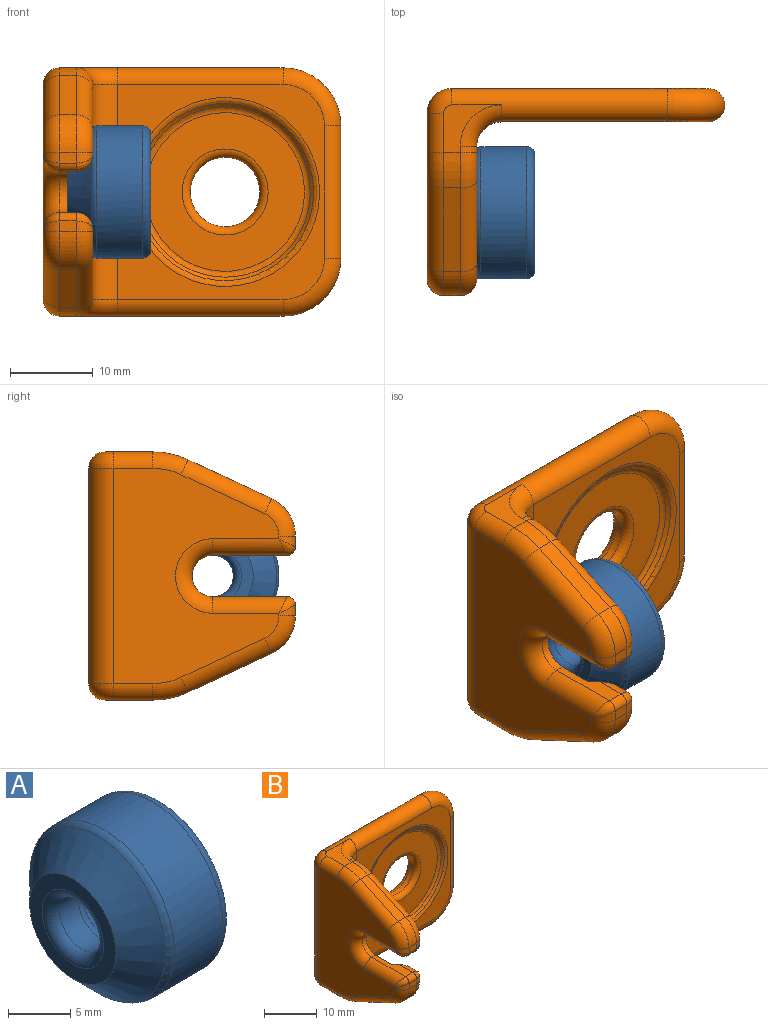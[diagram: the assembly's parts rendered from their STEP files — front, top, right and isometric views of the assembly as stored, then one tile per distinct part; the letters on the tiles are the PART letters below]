
ASSEMBLY  parts=2 mates=1
PART A: 12 faces, bbox 10x17.3x17.3 mm
  f0: cylinder r=2.5mm len=5mm, axis (-1,0,0), area 33.4mm2, adj f10,f11
  f1: cylinder r=8mm len=16mm, axis (-1,0,0), area 275.7mm2, adj f8,f9
  f2: plane 14x14mm, normal (1,0,0), area 21.2mm2, adj f7,f9
  f3: plane 9.8x9.8mm, normal (-1,0,0), area 36.9mm2, adj f4,f11
  f4: cone r=8mm half-angle=45deg, axis (1,0,0), area 157.2mm2, adj f3,f8
  f5: cylinder r=5.5mm len=11mm, axis (1,0,0), area 69.1mm2, adj f6,f7
  f6: torus R=2.5mm, axis (1,0,0), area 116.9mm2, adj f5,f10
  f7: torus R=6.5mm, axis (1,0,0), area 57.9mm2, adj f2,f5
  f8: torus R=7mm, axis (-1,0,0), area 39mm2, adj f1,f4
  f9: torus R=7mm, axis (1,0,0), area 75.4mm2, adj f1,f2
  f10: torus R=3.5mm, axis (-1,0,0), area 22.9mm2, adj f0,f6
  f11: torus R=3.5mm, axis (1,0,0), area 28.3mm2, adj f0,f3
PART B: 69 faces, bbox 36.6x25.5x31.7 mm
  f0: plane 16x13mm, normal (1,0,0), area 62.4mm2, adj f17,f18,f41,f42,f43,f44,f45,f47
  f1: plane 2x1.32mm, normal (0,-1,0), area 2.6mm2, adj f21,f23,f45,f60
  f2: plane 2x1.32mm, normal (0,-1,0), area 2.6mm2, adj f22,f24,f29,f57
  f3: plane 16x13mm, normal (1,0,0), area 62.4mm2, adj f17,f18,f27,f29,f30,f31,f32,f33
  f4: plane 7x5.78mm, normal (0,0,1), area 16.7mm2, adj f20,f33,f34,f35,f48,f49
  f5: plane 7x5.78mm, normal (0,0,-1), area 16.7mm2, adj f19,f39,f40,f41,f50,f52
  f6: plane 26x20mm, normal (-1,0,0), area 330.1mm2, adj f26,f49,f51,f52,f53,f54,f55,f56
  f7: plane 31x26mm, normal (0,1,0), area 710.3mm2, adj f26,f35,f36,f37,f38,f39,f66
  f8: plane 26x25mm, normal (0,-1,0), area 230mm2, adj f18,f35,f36,f37,f38,f39,f65
  f9: plane 19.17x19.17mm, normal (0,-1,0), area 203.7mm2, adj f67,f68
  f10: cylinder r=4.2mm len=8.4mm, axis (0,-1,0), area 26.4mm2, adj f66,f67
  f11: plane 10.1x4.72mm, normal (0,-0.42,-0.91), area 22.3mm2, adj f19,f21,f43,f56
  f12: plane 10.1x4.72mm, normal (0,-0.42,0.91), area 22.3mm2, adj f20,f22,f31,f53
  f13: plane 10x9.33mm, normal (1,0,0), area 44.8mm2, adj f14,f15,f16,f17
  f14: plane 9.05x2.05mm, normal (0,0,1), area 13.1mm2, adj f13,f15,f17,f23,f47,f64
  f15: cylinder r=2.5mm len=5mm, axis (1,0,0), area 7.9mm2, adj f13,f14,f16,f63
  f16: plane 9.05x2.05mm, normal (0,0,-1), area 13.1mm2, adj f13,f15,f17,f24,f27,f61
  f17: cone r=5mm half-angle=45deg, axis (1,0,0), area 148.8mm2, adj f0,f3,f13,f14,f16,f27,f47
  f18: cylinder r=3mm len=26mm, axis (0,0,-1), area 122.5mm2, adj f0,f3,f8,f34,f40
  f19: cylinder r=10mm len=4.23mm, axis (-1,0,0), area 8.7mm2, adj f5,f11,f42,f54
  f20: cylinder r=10mm len=4.23mm, axis (1,0,0), area 8.7mm2, adj f4,f12,f32,f51
  f21: cylinder r=5mm len=4.53mm, axis (1,0,0), area 11.3mm2, adj f1,f11,f44,f58
  f22: cylinder r=5mm len=4.53mm, axis (1,0,0), area 11.3mm2, adj f2,f12,f30,f55
  f23: cylinder r=1mm len=2mm, axis (-1,0,0), area 3.1mm2, adj f1,f14,f46,f62
  f24: cylinder r=1mm len=2mm, axis (1,0,0), area 3.1mm2, adj f2,f16,f28,f59
  f25: cone r=10mm half-angle=45deg, axis (0,-1,0), area 38.6mm2, adj f65,f68
  f26: cylinder r=3mm len=26mm, axis (0,0,-1), area 122.5mm2, adj f6,f7,f48,f50
  f27: cylinder r=2mm len=3.55mm, axis (0,1,0), area 6.7mm2, adj f3,f16,f17,f28
  f28: bspline ~2.1x2mm, area 3.3mm2, adj f24,f27,f29
  f29: cylinder r=2mm len=2mm, axis (0,0,-1), area 3mm2, adj f2,f3,f28,f30
  f30: torus R=3mm, axis (1,0,0), area 15.2mm2, adj f3,f22,f29,f31
  f31: cylinder r=2mm len=10.95mm, axis (0,-0.91,-0.42), area 35mm2, adj f3,f12,f30,f32
  f32: torus R=8mm, axis (1,0,0), area 12.7mm2, adj f3,f20,f31,f33
  f33: cylinder r=2mm len=2mm, axis (0,-1,0), area 2.5mm2, adj f3,f4,f32,f34
  f34: torus R=5mm, axis (0,0,1), area 18.4mm2, adj f4,f18,f33,f35
  f35: cylinder r=2mm len=26mm, axis (-1,0,0), area 144.5mm2, adj f4,f7,f8,f34,f36,f48
  f36: torus R=5mm, axis (0,1,0), area 61.9mm2, adj f7,f8,f35,f37
  f37: cylinder r=2mm len=16mm, axis (0,0,-1), area 100.5mm2, adj f7,f8,f36,f38
  f38: torus R=5mm, axis (0,1,0), area 61.9mm2, adj f7,f8,f37,f39
  f39: cylinder r=2mm len=26mm, axis (1,0,0), area 144.5mm2, adj f5,f7,f8,f38,f40,f50
  f40: torus R=5mm, axis (0,0,1), area 18.4mm2, adj f5,f18,f39,f41
  f41: cylinder r=2mm len=2mm, axis (0,1,0), area 2.5mm2, adj f0,f5,f40,f42
  f42: torus R=8mm, axis (1,0,0), area 12.7mm2, adj f0,f19,f41,f43
  f43: cylinder r=2mm len=10.95mm, axis (0,-0.91,0.42), area 35mm2, adj f0,f11,f42,f44
  f44: torus R=3mm, axis (1,0,0), area 15.2mm2, adj f0,f21,f43,f45
  f45: cylinder r=2mm len=2mm, axis (0,0,-1), area 3mm2, adj f0,f1,f44,f46
  f46: bspline ~2.1x2mm, area 3.3mm2, adj f23,f45,f47
  f47: cylinder r=2mm len=3.55mm, axis (0,-1,0), area 6.7mm2, adj f0,f14,f17,f46
  f48: torus R=1mm, axis (0,0,1), area 11.2mm2, adj f4,f26,f35,f49
  f49: cylinder r=2mm len=4.78mm, axis (0,1,0), area 15mm2, adj f4,f6,f48,f51
  f50: torus R=1mm, axis (0,0,1), area 11.2mm2, adj f5,f26,f39,f52
  f51: torus R=8mm, axis (1,0,0), area 12.7mm2, adj f6,f20,f49,f53
  f52: cylinder r=2mm len=4.78mm, axis (0,-1,0), area 15mm2, adj f5,f6,f50,f54
  f53: cylinder r=2mm len=10.95mm, axis (0,0.91,0.42), area 35mm2, adj f6,f12,f51,f55
  f54: torus R=8mm, axis (1,0,0), area 12.7mm2, adj f6,f19,f52,f56
  f55: torus R=3mm, axis (1,0,0), area 15.2mm2, adj f6,f22,f53,f57
  f56: cylinder r=2mm len=10.95mm, axis (0,-0.91,0.42), area 35mm2, adj f6,f11,f54,f58
  f57: cylinder r=2mm len=2mm, axis (0,0,1), area 3mm2, adj f2,f6,f55,f59
  f58: torus R=3mm, axis (1,0,0), area 15.2mm2, adj f6,f21,f56,f60
  f59: bspline ~2.1x2mm, area 3.3mm2, adj f24,f57,f61
  f60: cylinder r=2mm len=2mm, axis (0,0,1), area 3mm2, adj f1,f6,f58,f62
  f61: cylinder r=2mm len=9mm, axis (0,-1,0), area 27.1mm2, adj f6,f16,f59,f63
  f62: bspline ~2.1x2mm, area 3.3mm2, adj f23,f60,f64
  f63: torus R=4.5mm, axis (1,0,0), area 31.8mm2, adj f6,f15,f61,f64
  f64: cylinder r=2mm len=9mm, axis (0,1,0), area 27.1mm2, adj f6,f14,f62,f63
  f65: torus R=11.41mm, axis (0,1,0), area 54.5mm2, adj f8,f25
  f66: torus R=5.2mm, axis (0,-1,0), area 45mm2, adj f7,f10
  f67: torus R=5.2mm, axis (0,-1,0), area 45mm2, adj f9,f10
  f68: torus R=9.59mm, axis (0,-1,0), area 49.1mm2, adj f9,f25
PLACE A t=(-5.69,-0.97,-0.86)mm
PLACE B t=(-8.69,14.03,-15.86)mm
MATE cylindrical B.f17 <-> A.f0  axis (1,0,0) through (-5.69,-0.97,-0.86)mm
